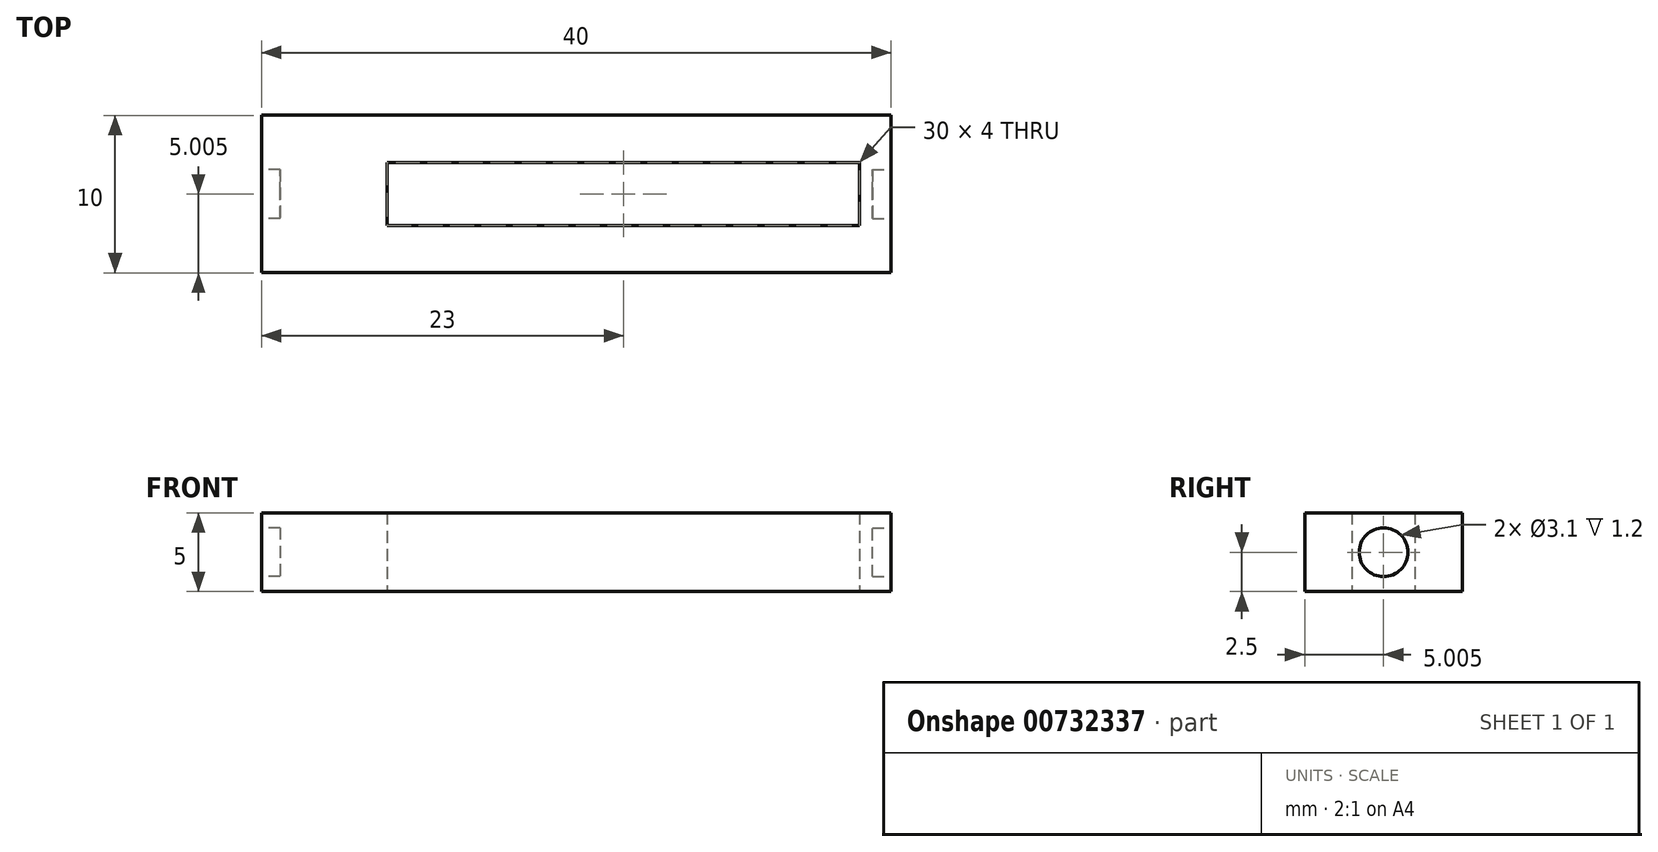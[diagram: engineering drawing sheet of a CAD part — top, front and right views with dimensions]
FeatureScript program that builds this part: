
annotation { "Feature Type Name" : "Feature", "Feature Type Description" : "" }
export const myFeature = defineFeature(function(context is Context, id is Id, definition is map)
    precondition{}
    {
        {
            var Q0;
            Q0=qCreatedBy(makeId("Top.planeOp"),FACE);
            var sketch = newSketch(context, id + "F0", { "sketchPlane" : qUnion([Q0])});
            skLineSegment(sketch, "E0.bottom", {"start": v(-25.07, 58.01) * mm, "end": v(14.93, 58.01) * mm});
            skLineSegment(sketch, "E0.top", {"start": v(-25.07, 48.01) * mm, "end": v(14.93, 48.01) * mm});
            skLineSegment(sketch, "E0.left", {"start": v(-25.07, 58.01) * mm, "end": v(-25.07, 48.01) * mm});
            skLineSegment(sketch, "E0.right", {"start": v(14.93, 58.01) * mm, "end": v(14.93, 48.01) * mm});
            skLineSegment(sketch, "E1.0", {"start": v(-17.07, 55.01) * mm, "end": v(12.93, 55.01) * mm});
            skLineSegment(sketch, "E2.0", {"start": v(-17.07, 51.01) * mm, "end": v(12.93, 51.01) * mm});
            skLineSegment(sketch, "E3.0", {"start": v(-17.07, 55.01) * mm, "end": v(-17.07, 51.01) * mm});
            skLineSegment(sketch, "E4.0", {"start": v(12.93, 55.01) * mm, "end": v(12.93, 51.01) * mm});
            skLineSegment(sketch, "E5", {"start": v(-17.07, 53.27) * mm, "end": v(-17.82, 53.27) * mm});
            skSolve(sketch);
        }
        {
            var Q0;
            Q0 = qSketchRegion(id + "F0", true);
            extrude(context, id + "F1", {"entities" : qUnion([Q0]), "depth" : 5 * mm, "offsetDistance" : 25 * mm});
        }
        {
            var Q0;
            Q0=makeQuery(id+"F1.opExtrude","SWEPT_FACE",FACE,{"disambiguationData":[OSD([sQuery(id+"F0.wireOp",EDGE,"E0.right")])]});
            var sketch = newSketch(context, id + "F2", { "sketchPlane" : qUnion([Q0])});
            skCircle(sketch, "E6", {"center": v(53.01, 2.5) * mm, "radius": 1.55 * mm});
            skSolve(sketch);
        }
        {
            var Q0;
            Q0 = qSketchRegion(id + "F2", true);
            extrude(context, id + "F3", {"entities" : qUnion([Q0]), "operationType" : NewBodyOperationType.REMOVE, "flatOperationType" : FlatOperationType.REMOVE, "oppositeDirection" : true, "depth" : 1.2 * mm, "offsetDistance" : 25 * mm, "domain" : OperationDomain.MODEL});
        }
        {
            var Q0;
            Q0=makeQuery(id+"F1.opExtrude","SWEPT_FACE",FACE,{"disambiguationData":[OSD([sQuery(id+"F0.wireOp",EDGE,"E0.left")])]});
            var sketch = newSketch(context, id + "F4", { "sketchPlane" : qUnion([Q0])});
            skCircle(sketch, "E7", {"center": v(-53.01, 2.5) * mm, "radius": 1.55 * mm});
            skSolve(sketch);
        }
        {
            var Q0;
            Q0 = qSketchRegion(id + "F4", true);
            extrude(context, id + "F5", {"entities" : qUnion([Q0]), "operationType" : NewBodyOperationType.REMOVE, "oppositeDirection" : true, "depth" : 1.2 * mm, "offsetDistance" : 25 * mm});
        }
    });
